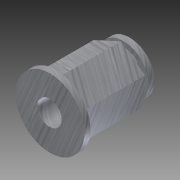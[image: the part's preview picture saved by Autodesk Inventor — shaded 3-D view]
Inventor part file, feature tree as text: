
AUTODESK INVENTOR PART (.ipt)
format: ipt  version: 2012 (Build 160160000, 160)  size: 138,752 bytes
history: native  units: in
note: dims shown in document units (in); Inventor stores cm internally (conversion verified against a paired STEP export)
features: extrude x5, sketch x5, reference x3, plane x1, projected_geometry x1
ambient origin geometry x8: Origin, YZ Plane, XZ Plane, XY Plane, X Axis, Y Axis, Z Axis, Center Point
bodies: Solid1 (feature_tree)
feature tree (15):
  extrude  "Extrusion1"  Depth=0.0591in TaperAngle=0.0deg
  extrude  "Extrusion2"  Depth=0.2362in
  plane  "Work Plane1"
  sketch  "Sketch3"  dims[d9=0.0591in d10=0.0in d13=0.0591in d14=0.0in]
  extrude  "Extrusion4"  Depth=0.0591in TaperAngle=0.0deg
  extrude  "Extrusion6"  Depth=0.3897in
  extrude  "Extrusion7"  [1 undecoded]
  sketch  "Sketch1"  dims[d0=0.0394in d1=0.0591in d2=0.0in]
  reference  "Reference1"
  sketch  "Sketch2"  dims[d3=0.7181in d4=0.0in d8=0.2362in]
  reference  "Reference2"
  reference  "Reference3"
  projected_geometry  "Projected Loop1"
  sketch  "Sketch4"  dims[d15=0.0591in d16=0.0in d17=0.3897in]
  sketch  "Sketch6"
note: 1 required parameter value undecoded (feature->parameter linkage not recoverable at this tier; creation-order binding heuristic only, values carry confidence <= 0.55)
